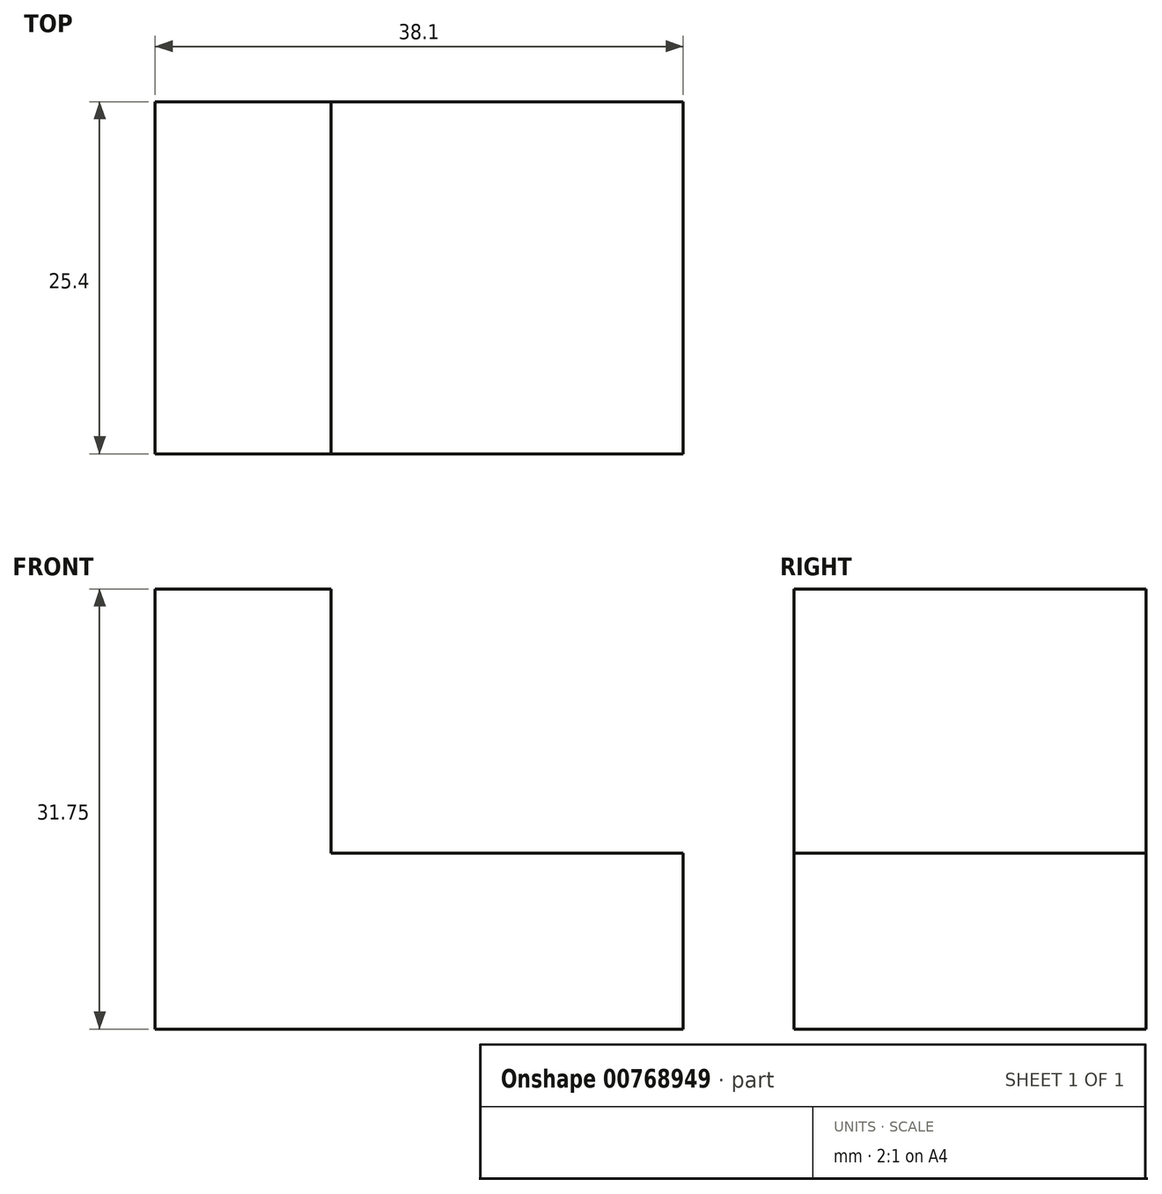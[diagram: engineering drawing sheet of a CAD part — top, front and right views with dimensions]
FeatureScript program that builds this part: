
annotation { "Feature Type Name" : "Feature", "Feature Type Description" : "" }
export const myFeature = defineFeature(function(context is Context, id is Id, definition is map)
    precondition{}
    {
        {
            var Q0;
            Q0=qCreatedBy(makeId("Front.planeOp"),FACE);
            var sketch = newSketch(context, id + "F0", { "sketchPlane" : qUnion([Q0])});
            skLineSegment(sketch, "E0", {"start": v(38.1, 0) * mm, "end": v(38.1, 12.7) * mm});
            skLineSegment(sketch, "E1", {"start": v(38.1, 12.7) * mm, "end": v(12.7, 12.7) * mm});
            skLineSegment(sketch, "E2", {"start": v(12.7, 12.7) * mm, "end": v(12.7, 31.75) * mm});
            skLineSegment(sketch, "E3", {"start": v(12.7, 31.75) * mm, "end": v(0, 31.75) * mm});
            skLineSegment(sketch, "E4", {"start": v(0, 31.75) * mm, "end": v(0, 0) * mm});
            skLineSegment(sketch, "E5", {"start": v(0, 0) * mm, "end": v(38.1, 0) * mm});
            skSolve(sketch);
        }
        {
            var Q0;
            Q0 = qSketchRegion(id + "F0", true);
            extrude(context, id + "F1", {"entities" : qUnion([Q0]), "depth" : 25.4 * mm, "offsetDistance" : 25.4 * mm});
        }
    });
